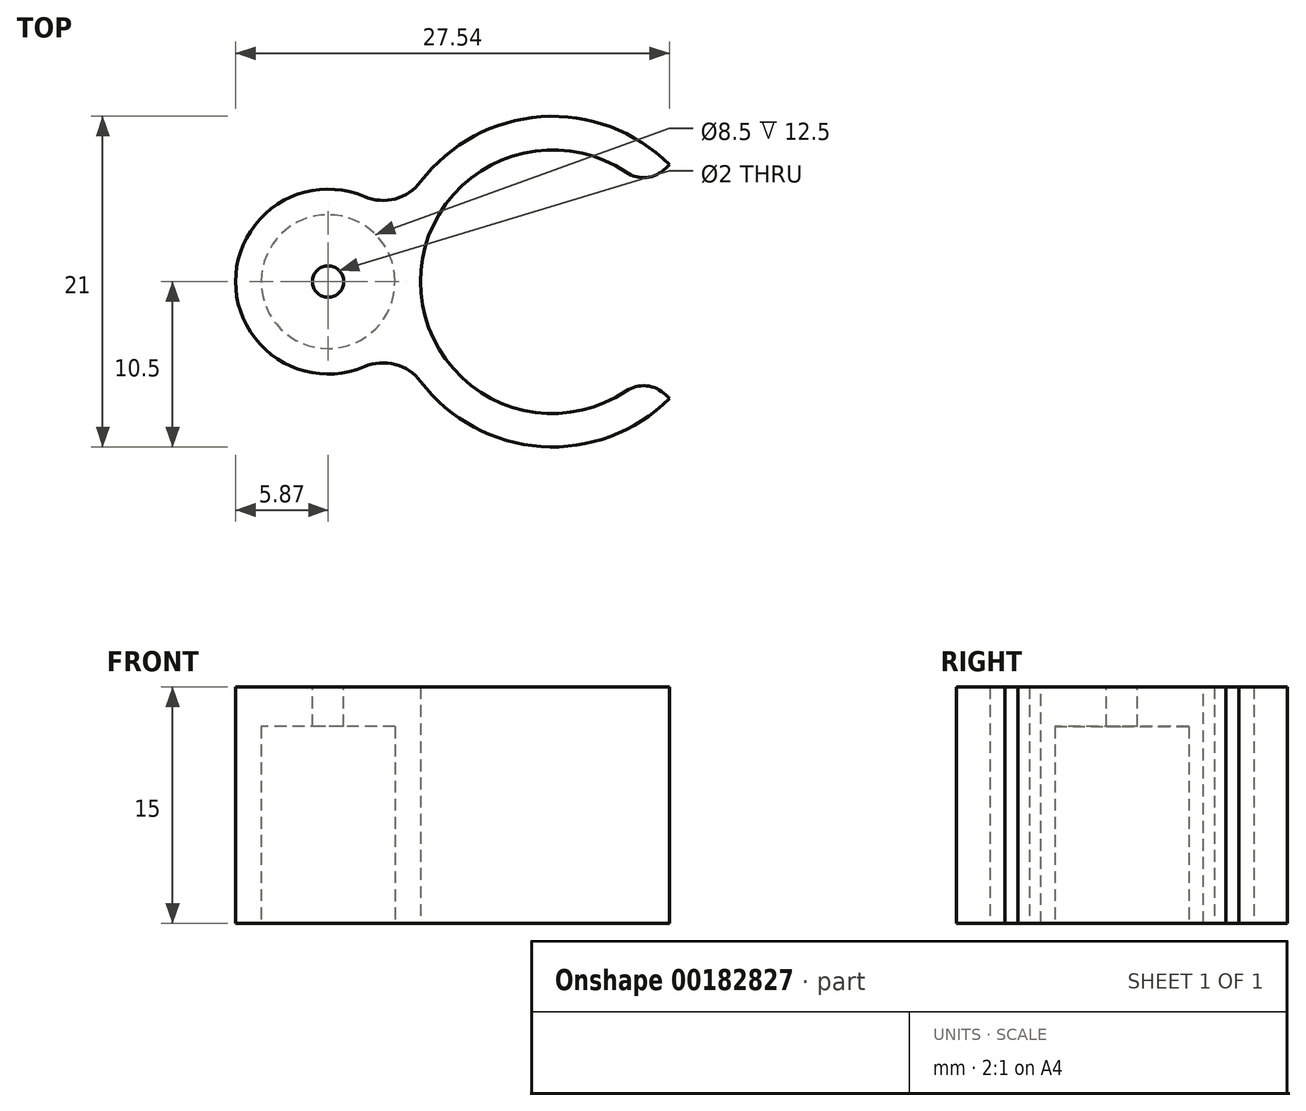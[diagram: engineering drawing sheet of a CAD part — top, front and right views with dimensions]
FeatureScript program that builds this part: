
annotation { "Feature Type Name" : "Feature", "Feature Type Description" : "" }
export const myFeature = defineFeature(function(context is Context, id is Id, definition is map)
    precondition{}
    {
        {
            var Q0;
            Q0=qCreatedBy(makeId("Top.planeOp"),FACE);
            var sketch = newSketch(context, id + "F0", { "sketchPlane" : qUnion([Q0])});
            skCircle(sketch, "E0", {"center": v(-14.25, 0) * mm, "radius": 4.25 * mm});
            skCircle(sketch, "E1", {"center": v(-14.25, 0) * mm, "radius": 5.88 * mm});
            skLineSegment(sketch, "E2", {"start": v(5.92, 5.92) * mm, "end": v(7.42, 7.42) * mm});
            skLineSegment(sketch, "E3", {"start": v(5.92, -5.92) * mm, "end": v(7.42, -7.42) * mm});
            skArc(sketch, "E4", {"start": v(5.92, 5.92) * mm, "mid": v(-8.38, 0) * mm, "end": v(5.92, -5.92) * mm});
            skArc(sketch, "E5", {"start": v(7.42, 7.42) * mm, "mid": v(-10.5, 0) * mm, "end": v(7.42, -7.42) * mm});
            skSolve(sketch);
        }
        {
            var Q0;
            Q0 = qSketchRegion(id + "F0", true);
            extrude(context, id + "F1", {"entities" : qUnion([Q0]), "depth" : 15 * mm});
        }
        {
            var Q0;
            Q0=makeQuery(id+"F1.opExtrude","SWEPT_EDGE",EDGE,{"disambiguationData":[OSD([sQuery(id+"F0.wireOp",EDGE,"E2"),sQuery(id+"F0.wireOp",EDGE,"E4")])]});
            var Q1;
            Q1=makeQuery(id+"F1.opExtrude","SWEPT_EDGE",EDGE,{"disambiguationData":[OSD([sQuery(id+"F0.wireOp",EDGE,"E3"),sQuery(id+"F0.wireOp",EDGE,"E4")])]});
            fillet(context, id + "F2", {"entities" : qUnion([Q0, Q1]), "radius" : 2 * mm, "tangentPropagation" : true, "allowEdgeOverflow" : false});
        }
        {
            var Q0;
            Q0=makeQuery(id+"F1.opExtrude","CAP_FACE",FACE,{"disambiguationData":[OSD([sQuery(id+"F0.wireOp",EDGE,"E0"),sQuery(id+"F0.wireOp",EDGE,"E1"),sQuery(id+"F0.wireOp",EDGE,"E2"),sQuery(id+"F0.wireOp",EDGE,"E3"),sQuery(id+"F0.wireOp",EDGE,"E4"),sQuery(id+"F0.wireOp",EDGE,"E5")])],"isStart":false});
            var sketch = newSketch(context, id + "F3", { "sketchPlane" : qUnion([Q0])});
            skCircle(sketch, "E6", {"center": v(-14.25, 0) * mm, "radius": 5.88 * mm});
            skSolve(sketch);
        }
        {
            var Q0;
            Q0 = qSketchRegion(id + "F3", true);
            extrude(context, id + "F4", {"entities" : qUnion([Q0]), "operationType" : NewBodyOperationType.ADD, "oppositeDirection" : true, "depth" : 2.5 * mm});
        }
        {
            var Q0;
            {var subQ0=sQuery(id+"F0.wireOp",EDGE,"E5");var subQ1=sQuery(id+"F0.wireOp",EDGE,"E1");Q0=makeQuery(id+"F1.opExtrude","SWEPT_EDGE",EDGE,{"disambiguationData":[OSD([subQ1,subQ0]),TDD([makeQuery(id+"F0.imprint","INTERSECT",VERTEX,{"disambiguationData":[OD(0.0)],"derivedFrom":[subQ1,subQ0]})])]});}
            var Q1;
            {var subQ0=sQuery(id+"F0.wireOp",EDGE,"E5");var subQ1=sQuery(id+"F0.wireOp",EDGE,"E1");Q1=makeQuery(id+"F1.opExtrude","SWEPT_EDGE",EDGE,{"disambiguationData":[OSD([subQ1,subQ0]),TDD([makeQuery(id+"F0.imprint","INTERSECT",VERTEX,{"disambiguationData":[OD(1.0)],"derivedFrom":[subQ1,subQ0]})])]});}
            fillet(context, id + "F5", {"entities" : qUnion([Q0, Q1]), "radius" : 3 * mm, "tangentPropagation" : true, "allowEdgeOverflow" : false});
        }
        {
            var Q0;
            Q0=makeQuery(id+"F4.boolean.opBoolean","MERGE",FACE,{"derivedFrom":[makeQuery(id+"F1.opExtrude","CAP_FACE",FACE,{"disambiguationData":[OSD([sQuery(id+"F0.wireOp",EDGE,"E0"),sQuery(id+"F0.wireOp",EDGE,"E1"),sQuery(id+"F0.wireOp",EDGE,"E2"),sQuery(id+"F0.wireOp",EDGE,"E3"),sQuery(id+"F0.wireOp",EDGE,"E4"),sQuery(id+"F0.wireOp",EDGE,"E5")])],"isStart":false}),makeQuery(id+"F4.opExtrude","CAP_FACE",FACE,{"disambiguationData":[OSD([sQuery(id+"F3.wireOp",EDGE,"E6")])],"isStart":true})]});
            var sketch = newSketch(context, id + "F6", { "sketchPlane" : qUnion([Q0])});
            skPoint(sketch, "E7", {"position": v(-14.25, 0) * mm});
            skSolve(sketch);
        }
        {
            var Q0;
            Q0=sQuery(id+"F6.wireOp",VERTEX,"E7");
            var Q1;
            Q1=makeQuery(id+"F1.opExtrude","SWEPT_BODY",BODY,{"disambiguationData":[OSD([sQuery(id+"F0.wireOp",EDGE,"E0"),sQuery(id+"F0.wireOp",EDGE,"E1"),sQuery(id+"F0.wireOp",EDGE,"E2"),sQuery(id+"F0.wireOp",EDGE,"E3"),sQuery(id+"F0.wireOp",EDGE,"E4"),sQuery(id+"F0.wireOp",EDGE,"E5")])]});
            hole(context, id + "F7", {"style" : HoleStyle.SIMPLE, "endStyle" : HoleEndStyle.THROUGH, "holeDiameter" : 2 * mm, "startFromSketch" : true, "locations" : qUnion([Q0]), "scope" : qUnion([Q1]), "isTappedThrough" : true});
        }
    });
